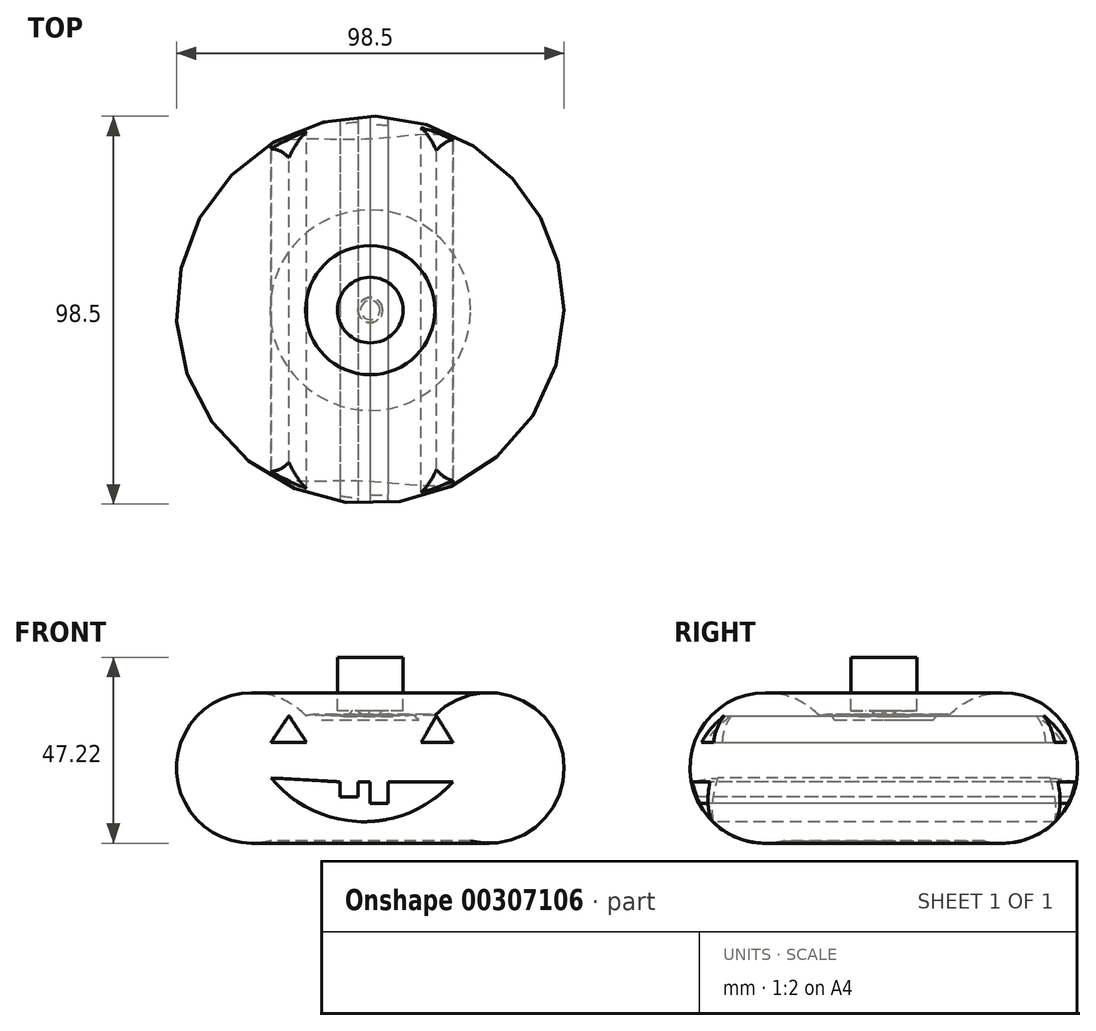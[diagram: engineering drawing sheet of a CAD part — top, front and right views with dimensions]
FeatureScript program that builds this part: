
annotation { "Feature Type Name" : "Feature", "Feature Type Description" : "" }
export const myFeature = defineFeature(function(context is Context, id is Id, definition is map)
    precondition{}
    {
        {
            var Q0;
            Q0=qCreatedBy(makeId("Front.planeOp"),FACE);
            var sketch = newSketch(context, id + "F0", { "sketchPlane" : qUnion([Q0])});
            skLineSegment(sketch, "E0", {"start": v(0, 85.18) * mm, "end": v(0, -87.43) * mm});
            skLineSegment(sketch, "E1", {"start": v(0, 0) * mm, "end": v(25.47, 0) * mm});
            skArc(sketch, "E2", {"start": v(25.47, 0) * mm, "mid": v(48.52, 23.78) * mm, "end": v(16.4, 31.87) * mm});
            skFitSpline(sketch, "E3", {"points": [v(16.4, 31.87) * mm, v(13.5, 31.87) * mm, v(12.4, 30.77) * mm, v(11.18, 31.87) * mm, v(10.09, 31.87) * mm, v(7.78, 31.87) * mm, v(5.72, 31.87) * mm, v(4.62, 33.08) * mm, v(4.26, 31.87) * mm, v(2.68, 31.87) * mm, v(2.44, 31.87) * mm, v(3.4, 33.45) * mm, v(1.34, 31.87) * mm, v(0, 33.08) * mm, v(0, 31.87) * mm], "startDerivative": vector(-35.02, 7.72) * mm, "endDerivative": vector(3.24, -30.95) * mm});
            skSolve(sketch);
        }
        {
            var Q0;
            {var subQ1=sQuery(id+"F0.wireOp",EDGE,"E1");Q0=makeQuery(id+"F0.imprint","IMPRINT",FACE,{"disambiguationData":[TD([[makeQuery(id+"F0.imprint","IMPRINT",EDGE,{"derivedFrom":subQ1}),1.0]])]});}
            var Q1;
            Q1=sQuery(id+"F0.wireOp",EDGE,"E0");
            revolve(context, id + "F1", {"entities" : qUnion([Q0]), "axis" : qUnion([Q1]), "revolveType" : RevolveType.FULL});
        }
        {
            var Q0;
            Q0=qCreatedBy(makeId("Right.planeOp"),FACE);
            var sketch = newSketch(context, id + "F2", { "sketchPlane" : qUnion([Q0])});
            skLineSegment(sketch, "E4", {"start": v(0, 33.1) * mm, "end": v(-8.34, 33.1) * mm});
            skLineSegment(sketch, "E5", {"start": v(-8.34, 33.1) * mm, "end": v(-8.34, 46.64) * mm});
            skLineSegment(sketch, "E6", {"start": v(-8.34, 46.64) * mm, "end": v(0, 46.64) * mm});
            skLineSegment(sketch, "E7", {"start": v(0, 46.64) * mm, "end": v(0, 33.1) * mm});
            skSolve(sketch);
        }
        {
            var Q0;
            Q0=qCreatedBy(makeId("Front.planeOp"),FACE);
            var sketch = newSketch(context, id + "F3", { "sketchPlane" : qUnion([Q0])});
            skLineSegment(sketch, "E8", {"start": v(0, 76.24) * mm, "end": v(0, -12.4) * mm});
            skSolve(sketch);
        }
        {
            var Q0;
            Q0=makeQuery(id+"F2.imprint","IMPRINT",FACE,{"disambiguationData":[TD([[makeQuery(id+"F2.imprint","IMPRINT",EDGE,{"derivedFrom":sQuery(id+"F2.wireOp",EDGE,"E4")}),-1.0]])]});
            var Q1;
            Q1=sQuery(id+"F3.wireOp",EDGE,"E8");
            revolve(context, id + "F4", {"operationType" : NewBodyOperationType.ADD, "entities" : qUnion([Q0]), "axis" : qUnion([Q1]), "revolveType" : RevolveType.FULL});
        }
        {
            var Q0;
            Q0=qCreatedBy(makeId("Front.planeOp"),FACE);
            var sketch = newSketch(context, id + "F5", { "sketchPlane" : qUnion([Q0])});
            skLineSegment(sketch, "E9", {"start": v(-25.22, 25.05) * mm, "end": v(-20.69, 31.84) * mm});
            skLineSegment(sketch, "E10", {"start": v(-20.69, 31.84) * mm, "end": v(-16.16, 25.05) * mm});
            skLineSegment(sketch, "E11", {"start": v(-16.16, 25.05) * mm, "end": v(-25.22, 25.05) * mm});
            skLineSegment(sketch, "E12", {"start": v(12.93, 25.05) * mm, "end": v(16.81, 31.84) * mm});
            skLineSegment(sketch, "E13", {"start": v(16.81, 31.84) * mm, "end": v(21.01, 25.05) * mm});
            skLineSegment(sketch, "E14", {"start": v(21.01, 25.05) * mm, "end": v(12.93, 25.05) * mm});
            skSolve(sketch);
        }
        {
            var Q0;
            Q0 = qSketchRegion(id + "F5", true);
            extrude(context, id + "F6", {"entities" : qUnion([Q0]), "operationType" : NewBodyOperationType.REMOVE, "endBound" : BoundingType.SYMMETRIC, "depth" : 121.92 * mm});
        }
        {
            var Q0;
            Q0=qCreatedBy(makeId("Front.planeOp"),FACE);
            var sketch = newSketch(context, id + "F7", { "sketchPlane" : qUnion([Q0])});
            skArc(sketch, "E15", {"start": v(-25.22, 16) * mm, "mid": v(-2.32, 4.91) * mm, "end": v(21.01, 15.03) * mm});
            skLineSegment(sketch, "E16", {"start": v(-25.22, 16) * mm, "end": v(-7.65, 15.03) * mm});
            skLineSegment(sketch, "E17", {"start": v(-7.65, 15.03) * mm, "end": v(-7.65, 11.25) * mm});
            skLineSegment(sketch, "E18", {"start": v(-7.65, 11.25) * mm, "end": v(-3.13, 11.25) * mm});
            skLineSegment(sketch, "E19", {"start": v(-3.13, 11.25) * mm, "end": v(-3.13, 15.03) * mm});
            skLineSegment(sketch, "E20", {"start": v(-3.13, 15.03) * mm, "end": v(0, 15.03) * mm});
            skLineSegment(sketch, "E21", {"start": v(0, 15.03) * mm, "end": v(0, 9.61) * mm});
            skLineSegment(sketch, "E22", {"start": v(0, 9.61) * mm, "end": v(4.56, 9.61) * mm});
            skLineSegment(sketch, "E23", {"start": v(4.56, 9.61) * mm, "end": v(4.56, 15.03) * mm});
            skLineSegment(sketch, "E24", {"start": v(4.56, 15.03) * mm, "end": v(21.01, 15.03) * mm});
            skSolve(sketch);
        }
        {
            var Q0;
            Q0 = qSketchRegion(id + "F7", true);
            extrude(context, id + "F8", {"entities" : qUnion([Q0]), "operationType" : NewBodyOperationType.REMOVE, "endBound" : BoundingType.SYMMETRIC, "oppositeDirection" : true, "depth" : 127 * mm});
        }
    });
